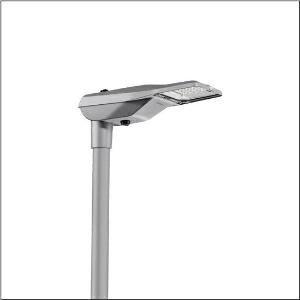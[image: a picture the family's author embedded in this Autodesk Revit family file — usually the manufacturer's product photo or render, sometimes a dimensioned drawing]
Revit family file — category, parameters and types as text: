
# Revit family: streetlight_sl_21_iq_micro___st1_0ab_5xe1m31y08db_79d8
name_source: partatom
category: Lighting Fixtures
units: mm (PartAtom-declared; Revit-internal decimal feet)

## family parameters
Cut with Voids When Loaded = No
Host = Face
Light Source = No
Part Type = Normal
Room Calculation Point = No
Round Connector Dimension = Use Diameter
Shared = No

## types (1)
- --- (1 x LED, 4490 lm, 39.1 W, 3000K)
    Apparent Load = 39 VA
    CIE Flux Codes = 38 73 97 100 100
    Color Rendering = 70
    Color Temperature = 3000K
    Default Elevation = 1800 mm
    Description = Streetlight SL 21 iQ micro, mast luminaire, primary light control with lens, of PMMA, primary optical cover: cover, of toughened safety glass, transparent, light distribution: ST1.0aB, light emission: direct distribution, primary light characteristic: asymmetric, installation type: post-top, side-entry, LED, High Power LED, rated luminous flux: 4.490lm, luminous efficacy: 115lm/W, light colour: 730, colour temperature: 3000K, control gear: iQ-Street Remote, D4i with power reduction, control: pre-setting: logarithmic dimming characteristic, Street-Remote, Auto-Match, Temp-Guard, Lumen-Switch, Night-Set, Smart-Wire, Light-Fading, Desk-Remote (wireless, voltage-free reading and setting of iQ features in the workshop via application-optimized NFC function/RFID function), optimised constant luminous flux control (CLO 2.0), mains connection: 220..240V, AC, 50/60Hz, start of lifetime: 39W, end of service life: 41W, reduction: 17W, luminaire housing, of diecast aluminium, powder-coated, Siteco® metallic grey (DB 702S), corrosivity category C5 high according to DIN EN ISO 12944, please order mast flange separately, inclination adjustable: 0°, 5°, 10°, 15°, sealing non-destructively replaceable, multi-level sealing system, length: 528mm, width: 235mm, height: 110mm, mast flange for spigot size: 42mm (side-entry): 5XC10008XM4, 60/48mm (side-entry/post-top): 5XC10108XM2, 76/60mm (side-entry/post-top): 5XC10108XM1, mounting height: 4..8m, Smart Interface below and above, protection rating (complete): IP66, insulation class (complete): insulation class II (safety insulation), certification: CE, ENEC, ENEC+, VDE, impact resistance: IK10, permissible operating ambient temperature for outdoor applications: -40..+50°C, standard-compliant lighting for roads and squares, packaging unit: 1 piece

Light Distribution: ST1.0aB
    Height = 110 mm
    Lamp = 1 x LED
    Lamp Light Flux = 4490 lm
    Lamp Power = 39.1 W
    Lamp count = 1
    Length = 528 mm
    Luminous efficacy = 115 lm/W
    Manufacturer = Siteco
    ModVariant = No
    Model = 5XE1M31Y08DB
    Number of Poles = 1
    OnlyDefault = Yes
    Power Factor = 1
    Product Name = Streetlight SL 21 iQ micro | ST1.0aB
    Product group = mast luminaire | pylon top
    ProductGroupID = 6100
    Protection Class = Protection class II
    Protection Degree = IP 66
    RLX_Detail_Level = 1
    RLX_Emergency_Light_Flux = 0 lm
    RLX_Emergency_Type = 0
    RLX_Emergency_Type_DB = No
    RlxData = <blob elided: 98473 chars, md5=2f3aaf20>
    Socket = socket
    Standby Power = 0 W
    System Light Flux = 4490 lm
    System Power = 39 W
    Type Comments = factory setting: luminous flux: 100 % | dim-lin: 254 | 765 mA
    Type Image = l_1007239.jpg
    URL = http://relux.com
    VarID = @adj_116539
    Voltage = 0 V
    Weight = 0.00 kg
    Width = 235 mm

## geometry (parser evidence)
native form markers: Blend x4, Sweep x12
no freeform markers — native parametric forms only
